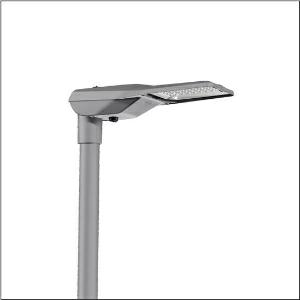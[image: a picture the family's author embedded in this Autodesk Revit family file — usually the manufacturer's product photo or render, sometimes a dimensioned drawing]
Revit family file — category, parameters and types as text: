
# Revit family: streetlight_sl_21_iq_mini___st1_0a_5xe2d51y08jb_5dfa
name_source: partatom
category: Lighting Fixtures
units: mm (PartAtom-declared; Revit-internal decimal feet)

## family parameters
Cut with Voids When Loaded = No
Host = Face
Light Source = No
Part Type = Normal
Room Calculation Point = No
Round Connector Dimension = Use Diameter
Shared = No

## types (1)
- --- (1 x LED, 9850 lm, 72.5 W, 3000K)
    Apparent Load = 73 VA
    CIE Flux Codes = 40 73 97 100 100
    Color Rendering = 80
    Color Temperature = 3000K
    Default Elevation = 1800 mm
    Description = Streetlight SL 21 iQ mini, mast luminaire, primary light control with lens, of PMMA, primary optical cover: cover, of toughened safety glass, transparent, light distribution: ST1.0a, light emission: direct distribution, primary light characteristic: asymmetric, installation type: post-top, side-entry, LED, High Power LED, rated luminous flux: 9.850lm, luminous efficacy: 136lm/W, light colour: 830, colour temperature: 3000K, control: presetting dimming logarithmic, Street-Remote, Auto-Match, Temp-Guard, Lumen-Switch, Night-Set, Smart-Wire, Light-Fading, Desk-Remote (wireless, voltage-free reading and setting of iQ features in the workshop via application-optimized NFC function/RFID function), optimised constant luminous flux control (CLO 2.0), mains connection: 220..240V, AC, 50/60Hz, start of lifetime: 73W, end of service life: 76W, reduction: 33W, luminaire housing, of diecast aluminium, powder-coated, Siteco® metallic grey (DB 702S), corrosivity category C5 mid according to DIN EN ISO 12944, please order mast flange separately, inclination adjustable: 0°, 5°, 10°, 15°, sealing non-destructively replaceable, multi-level sealing system, length: 628mm, width: 235mm, height: 110mm, mast flange for spigot size: 42mm (side-entry): 5XC10008XM4, 60/48mm (side-entry/post-top): 5XC10108XM2, 76/60mm (side-entry/post-top): 5XC10108XM1, Smart Interface below and above, protection rating (complete): IP66, insulation class (complete): insulation class II (safety insulation), certification: CE, ENEC, ENEC+, VDE, impact resistance: IK09, permissible operating ambient temperature for outdoor applications: -40..+50°C, standard-compliant lighting for roads and squares, packaging unit: 1 piece

Light Distribution: ST1.0a
    Height = 110 mm
    Lamp = 1 x LED
    Lamp Light Flux = 9850 lm
    Lamp Power = 72.5 W
    Lamp count = 1
    Length = 625 mm
    Luminous efficacy = 136 lm/W
    Manufacturer = Siteco
    ModVariant = No
    Model = 5XE2D51Y08JB
    Number of Poles = 1
    OnlyDefault = Yes
    Power Factor = 1
    Product Name = Streetlight SL 21 iQ mini | ST1.0a
    Product group = mast luminaire | pylon top
    ProductGroupID = 6100
    Protection Class = Protection class II
    Protection Degree = IP 66
    RLX_Detail_Level = 1
    RLX_Emergency_Light_Flux = 0 lm
    RLX_Emergency_Type = 0
    RLX_Emergency_Type_DB = No
    RlxData = <blob elided: 92325 chars, md5=4cedf98f>
    Socket = socket
    Standby Power = 0 W
    System Light Flux = 9850 lm
    System Power = 73 W
    Type Comments = factory setting: luminous flux: 100 % | dim-lin: 254 | 755 mA
    Type Image = l_1003514.jpg
    URL = http://relux.com
    VarID = @adj_044073
    Voltage = 0 V
    Weight = 0.00 kg
    Width = 234 mm

## geometry (parser evidence)
native form markers: Blend x4, Sweep x11
no freeform markers — native parametric forms only
